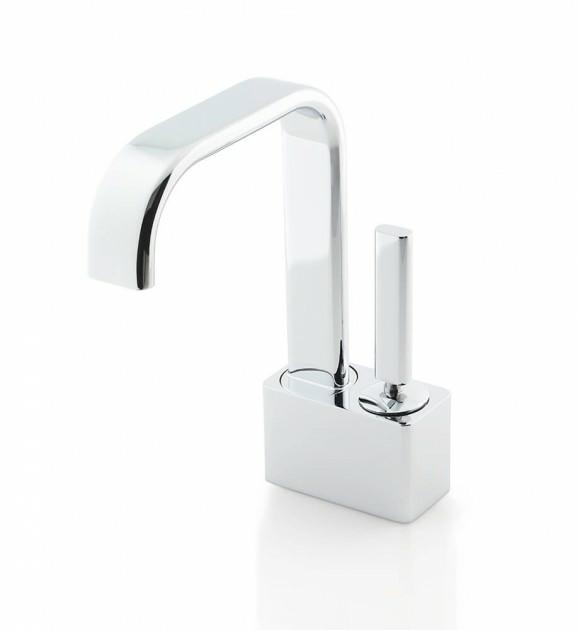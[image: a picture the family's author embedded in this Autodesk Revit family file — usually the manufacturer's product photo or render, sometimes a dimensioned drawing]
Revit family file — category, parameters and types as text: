
# Revit family: BN1010001_LVM MEDIO MONO_BORNEO
name_source: partatom
category: Aparatos sanitarios
revit_build: Autodesk Revit 2018 (Build: 20170223_1515(x64)
units: mm (PartAtom-declared; Revit-internal decimal feet)

## family parameters
Anfitrión = Cara
Compartido = No
Corte con vacíos al cargar = No
Cota de conector redondo = Diámetro de uso
Número OmniClass = 23.45.55.17
Punto de cálculo de habitación = No
Tipo de pieza = Normal
Título OmniClass = Mixing Faucets

## types (1)
- BN1010001_LVM MEDIO MONO_BORNEO
    Consumo de Agua = 7,6 l/m
    Elevación por defecto = 1219 mm
    Fabricante = American Standard
    Garantía = 10 años
    Imagen de tipo = <Ninguno>
    Material = Latón
    Modelo = Borneo Grifería Lavamanos de Sobreponer
    Presion Recomendada = 72.5 PSI
    Referencia = BN1010001
    Tipo = Grifería Lavamanos de Sobreponer
    URL = https://www.americanstandard.com.co

## geometry (parser evidence)
native form markers: Sweep x2
no freeform markers — native parametric forms only
